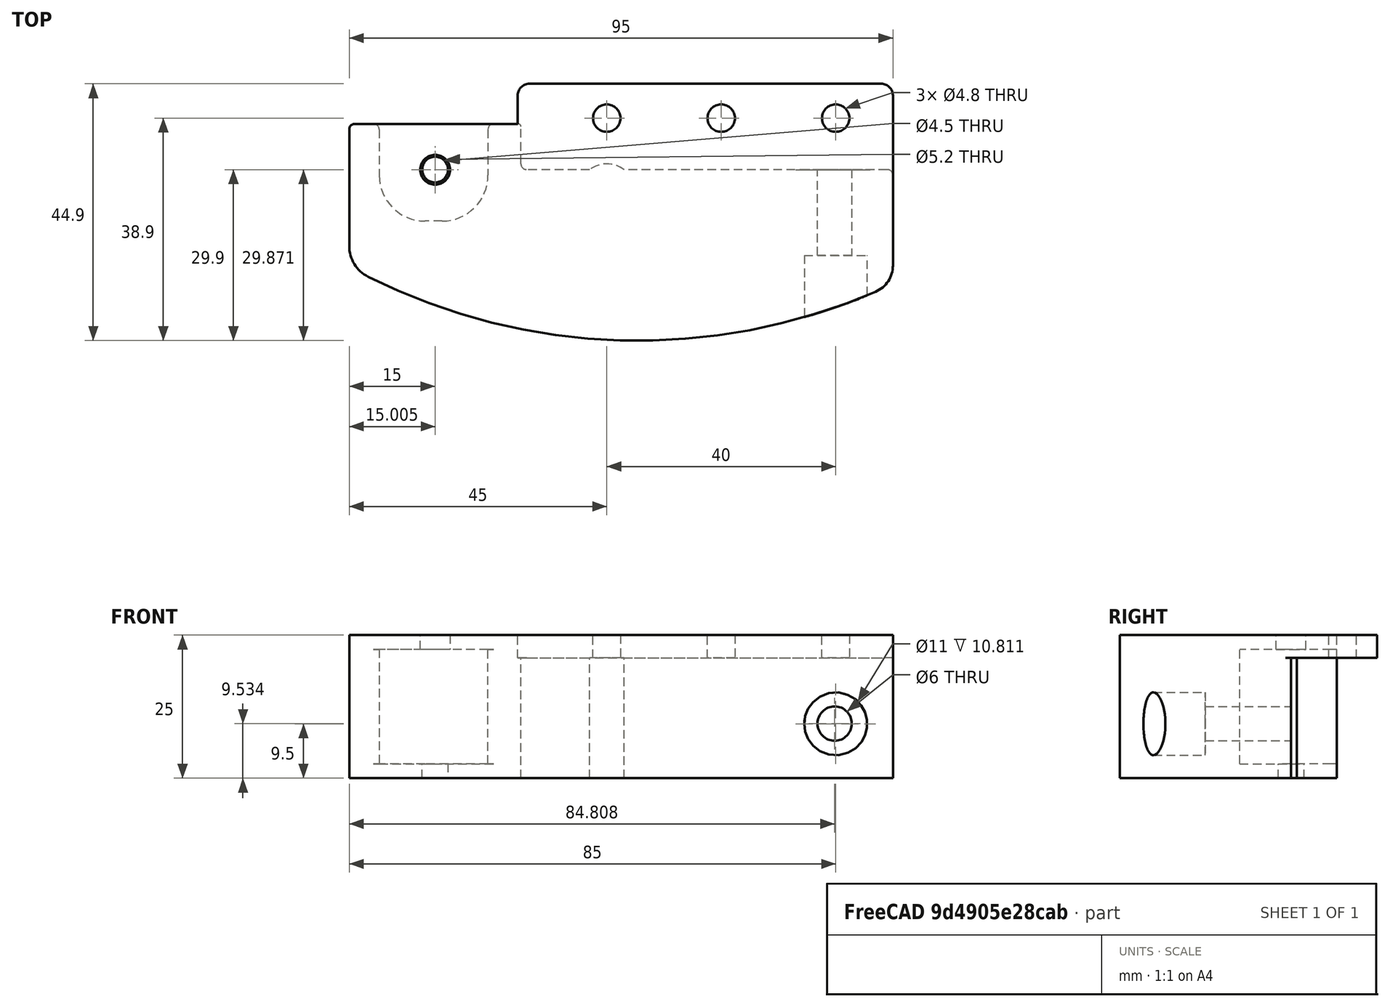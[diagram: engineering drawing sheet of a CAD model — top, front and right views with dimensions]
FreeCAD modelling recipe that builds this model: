
FCSTD DOCUMENT  (FreeCAD 0.19R)
Label: FrontTensioner
License: All rights reserved
LicenseURL: http://en.wikipedia.org/wiki/All_rights_reserved
objects: Sketcher::SketchObject×9, PartDesign::Fillet×8, PartDesign::Pocket×5, PartDesign::Pad×4, PartDesign::Body×1, Mesh::Feature×1
note: 44 computed .brp shape members not serialized (recipe doc carries the construction recipe); baked Part::Feature solids carry a one-line shape summary decoded from their .brp

FEATURE [Sketcher::SketchObject] Sketch  label="Body001"
  FullyConstrained = true
  MapMode = 5
  Support = -> [XY_Plane]
  sketch-geometry (7):
    g0: LineSegment StartX=30 StartY=0 StartZ=0 EndX=30 EndY=-20 EndZ=0
    g1: LineSegment StartX=-65 StartY=8 StartZ=0 EndX=-65 EndY=-17 EndZ=0
    g2: ArcOfCircle CenterX=-14.54 CenterY=75.2333 CenterZ=0 NormalX=0 NormalY=0 NormalZ=1 AngleXU=0 Radius=105.134 StartAngle=4.21178 EndAngle=5.14986
    g3: LineSegment StartX=30 StartY=0 StartZ=0 EndX=-35 EndY=0 EndZ=0
    g4: LineSegment StartX=-35 StartY=0 StartZ=0 EndX=-35 EndY=8 EndZ=0
    g5: LineSegment StartX=-35 StartY=8 StartZ=0 EndX=-65 EndY=8 EndZ=0
    g6: LineSegment StartX=-30 StartY=0 StartZ=0 EndX=30 EndY=0 EndZ=0
  constraints (23):
    c: PointOnObject(g0,g-1)
    c: Vertical(g0)
    c: Coincident(g2,g1)
    c: Coincident(g2,g0)
    c: Vertical(g1)
    c: Coincident(g0,g3)
    c: PointOnObject(g3,g-1)
    c: Coincident(g3,g4)
    c: Vertical(g4)
    c: Coincident(g4,g5)
    c: Horizontal(g5)
    c: Coincident(g1,g5)
    c: Distance(g4) = 8
    c: PointOnObject(g6,g3)
    c: PointOnObject(g6,g3)
    c: DistanceX(g6) = 30
    c: DistanceX(g6) = -30
    c: DistanceX(g3) = -35
    c: Distance(g5) = 30
    c: DistanceX(g0) = 30
    c: Distance(g0) = 20
    c: Distance(g1) = 25
    c: DistanceX(g2) = -14.54
FEATURE [PartDesign::Pad] Pad
  Direction = (1,1,1)
  Length = 25
  Length2 = 100
  Profile = -> Sketch
  Type = 0
FEATURE [Sketcher::SketchObject] Sketch001
  FullyConstrained = true
  MapMode = 5
  Placement = pos=(0,0,0) rot=(0,0.707107,0.707107;3.14159rad)
  Support = -> [Pad]
  sketch-geometry (1):
    g0: Circle CenterX=-20 CenterY=9.5 CenterZ=0 NormalX=0 NormalY=0 NormalZ=1 AngleXU=0 Radius=5.5
  constraints (3):
    c: DistanceX(g0) = -20
    c: DistanceY(g0) = 9.5
    c: Diameter(g0) = 11
FEATURE [PartDesign::Pocket] Pocket
  BaseFeature = -> Pad
  Length = 5
  Length2 = 100
  Profile = -> Sketch001
  Type = 1
FEATURE [Sketcher::SketchObject] Sketch002  label="FulcrumHump"
  FullyConstrained = true
  MapMode = 5
  Placement = pos=(0,0,25) rot=(0,0,1;0rad)
  Support = -> [Pocket]
  sketch-geometry (1):
    g0: Circle CenterX=-20 CenterY=-4 CenterZ=0 NormalX=0 NormalY=0 NormalZ=1 AngleXU=0 Radius=5
  constraints (3):
    c: Diameter(g0) = 10
    c: DistanceX(g0) = -20
    c: DistanceY(g0) = -4
FEATURE [PartDesign::Pad] Pad001
  BaseFeature = -> Pocket
  Direction = (1,1,1)
  Length = 25
  Length2 = 100
  Profile = -> Sketch002
  Reversed = true
  Type = 0
FEATURE [Sketcher::SketchObject] Sketch003
  FullyConstrained = false
  MapMode = 5
  Placement = pos=(0,8,0) rot=(0,0.707107,0.707107;3.14159rad)
  Support = -> [Pad001]
  sketch-geometry (4):
    g0: LineSegment StartX=40.76 StartY=22.5 StartZ=0 EndX=59.76 EndY=22.5 EndZ=0
    g1: LineSegment StartX=59.76 StartY=22.5 StartZ=0 EndX=59.76 EndY=2.5 EndZ=0
    g2: LineSegment StartX=59.76 StartY=2.5 StartZ=0 EndX=40.76 EndY=2.5 EndZ=0
    g3: LineSegment StartX=40.76 StartY=2.5 StartZ=0 EndX=40.76 EndY=22.5 EndZ=0
  constraints (11):
    c: Coincident(g0,g1)
    c: Coincident(g1,g2)
    c: Coincident(g2,g3)
    c: Coincident(g3,g0)
    c: Horizontal(g0)
    c: Horizontal(g2)
    c: Vertical(g1)
    c: Vertical(g3)
    c: Distance(g0) = 19
    c: DistanceY(g1,g1) = 20
    c: DistanceY(g1) = 2.5
FEATURE [PartDesign::Pocket] Pocket001
  BaseFeature = -> Pad001
  Length = 17
  Length2 = 100
  Profile = -> Sketch003
  Type = 0
FEATURE [Sketcher::SketchObject] Sketch004  label="mountshelf"
  FullyConstrained = false
  MapMode = 5
  Placement = pos=(0,0,25) rot=(0,0,1;0rad)
  Support = -> [Pocket001]
  sketch-geometry (4):
    g0: LineSegment StartX=-35.5567 StartY=15 StartZ=0 EndX=30 EndY=15 EndZ=0
    g1: LineSegment StartX=30 StartY=15 StartZ=0 EndX=30 EndY=-3.74646 EndZ=0
    g2: LineSegment StartX=30 StartY=-3.74646 StartZ=0 EndX=-35.5567 EndY=-3.74646 EndZ=0
    g3: LineSegment StartX=-35.5567 StartY=-3.74646 StartZ=0 EndX=-35.5567 EndY=15 EndZ=0
  constraints (10):
    c: Coincident(g0,g1)
    c: Coincident(g1,g2)
    c: Coincident(g2,g3)
    c: Coincident(g3,g0)
    c: Horizontal(g0)
    c: Horizontal(g2)
    c: Vertical(g1)
    c: Vertical(g3)
    c: DistanceX(g-1,g0) = 30
    c: DistanceY(g0) = 15
FEATURE [PartDesign::Pad] Pad002
  BaseFeature = -> Pocket001
  Direction = (1,1,1)
  Length = 4
  Length2 = 100
  Profile = -> Sketch004
  Reversed = true
  Type = 0
FEATURE [Sketcher::SketchObject] Sketch005  label="mountholes"
  FullyConstrained = true
  MapMode = 5
  Placement = pos=(0,0,25) rot=(0,0,1;0rad)
  Support = -> [Pad002]
  sketch-geometry (3):
    g0: Circle CenterX=-20 CenterY=9 CenterZ=0 NormalX=0 NormalY=0 NormalZ=1 AngleXU=0 Radius=2.4
    g1: Circle CenterX=0 CenterY=9 CenterZ=0 NormalX=0 NormalY=0 NormalZ=1 AngleXU=0 Radius=2.4
    g2: Circle CenterX=20 CenterY=9 CenterZ=0 NormalX=0 NormalY=0 NormalZ=1 AngleXU=0 Radius=2.4
  constraints (8):
    c: Diameter(g2) = 4.8
    c: Equal(g2,g1)
    c: Equal(g2,g0)
    c: PointOnObject(g1,g-2)
    c: DistanceX(g0) = -20
    c: Symmetric(g0,g2,g-2)
    c: DistanceY(g0) = 9
    c: DistanceY(g1) = 9
FEATURE [PartDesign::Pocket] Pocket002
  BaseFeature = -> Pad002
  Length = 5
  Length2 = 100
  Profile = -> Sketch005
  Type = 1
FEATURE [Sketcher::SketchObject] Sketch006  label="PulleyHole"
  FullyConstrained = true
  MapMode = 5
  Placement = pos=(0,0,25) rot=(0,0,1;0rad)
  Support = -> [Pocket002]
  sketch-geometry (1):
    g0: Circle CenterX=-50 CenterY=0 CenterZ=0 NormalX=0 NormalY=0 NormalZ=1 AngleXU=0 Radius=2.25
  constraints (3):
    c: Diameter(g0) = 4.5
    c: PointOnObject(g0,g-1)
    c: DistanceX(g0) = -50
FEATURE [PartDesign::Pocket] Pocket003
  BaseFeature = -> Pocket002
  Length = 5
  Length2 = 100
  Profile = -> Sketch006
  Type = 1
FEATURE [Sketcher::SketchObject] Sketch007  label="TensionBoltBore"
  FullyConstrained = false
  MapMode = 5
  Placement = pos=(0,0,0) rot=(1,0,0;1.5708rad)
  Support = -> [XZ_Plane]
  sketch-geometry (2):
    g0: Circle CenterX=19.8085 CenterY=9.53348 CenterZ=0 NormalX=0 NormalY=0 NormalZ=1 AngleXU=0 Radius=7
    g1: Circle CenterX=19.8085 CenterY=9.53348 CenterZ=0 NormalX=0 NormalY=0 NormalZ=1 AngleXU=0 Radius=3
  constraints (3):
    c: Coincident(g1,g0)
    c: Diameter(g1) = 6
    c: Diameter(g0) = 14
FEATURE [PartDesign::Pad] Pad003
  BaseFeature = -> Pocket003
  Direction = (1,1,1)
  Length = 15
  Length2 = 100
  Profile = -> Sketch007
  Type = 0
FEATURE [PartDesign::Fillet] Fillet
  Base = -> Pad003 [Edge16]
  BaseFeature = -> Pad003
  Radius = 6
  SupportTransform = false
FEATURE [PartDesign::Fillet] Fillet001
  Base = -> Fillet [Edge13]
  BaseFeature = -> Fillet
  Radius = 5
  SupportTransform = false
FEATURE [PartDesign::Fillet] Fillet002
  Base = -> Fillet001 [Edge65,Edge85]
  BaseFeature = -> Fillet001
  Radius = 2
  SupportTransform = false
FEATURE [PartDesign::Fillet] Fillet003
  Base = -> Fillet002 [Edge20,Edge25,Edge24]
  BaseFeature = -> Fillet002
  Radius = 1
  SupportTransform = false
FEATURE [PartDesign::Fillet] Fillet004
  Base = -> Fillet003 [Edge107,Edge108]
  BaseFeature = -> Fillet003
  Radius = 8
  SupportTransform = false
FEATURE [Sketcher::SketchObject] Sketch008
  FullyConstrained = false
  MapMode = 5
  Placement = pos=(0,0,25) rot=(0,0,1;0rad)
  Support = -> [Fillet004]
  sketch-geometry (1):
    g0: Circle CenterX=-49.9948 CenterY=-0.028644 CenterZ=0 NormalX=0 NormalY=0 NormalZ=1 AngleXU=0 Radius=2.6
  constraints (1):
    c: Diameter(g0) = 5.2
FEATURE [PartDesign::Pocket] Pocket004
  BaseFeature = -> Fillet004
  Length = 7
  Length2 = 100
  Profile = -> Sketch008
  Type = 0
FEATURE [PartDesign::Fillet] Fillet005
  Base = -> Pocket004 [Edge85]
  BaseFeature = -> Pocket004
  Radius = 1
  SupportTransform = false
FEATURE [PartDesign::Fillet] Fillet006
  Base = -> Fillet005 [Edge35]
  BaseFeature = -> Fillet005
  Radius = 1
  SupportTransform = false
FEATURE [PartDesign::Fillet] Fillet007
  Base = -> Fillet006 [Edge17]
  BaseFeature = -> Fillet006
  Radius = 0.5
  SupportTransform = false
FEATURE [PartDesign::Body] Body
  Group = -> [Sketch,Pad,Sketch001,Pocket,Sketch002,Pad001,Sketch003,Pocket001,Sketch004,Pad002,Sketch005,Pocket002,Sketch006,Pocket003,Sketch007,Pad003,Fillet,Fillet001,Fillet002,Fillet003,Fillet004,Sketch008,Pocket004,Fillet005,Fillet006,Fillet007]
  Origin = -> Origin
  Tip = -> Fillet007
FEATURE [Mesh::Feature] Mesh  label="Fillet007 (Meshed)"
